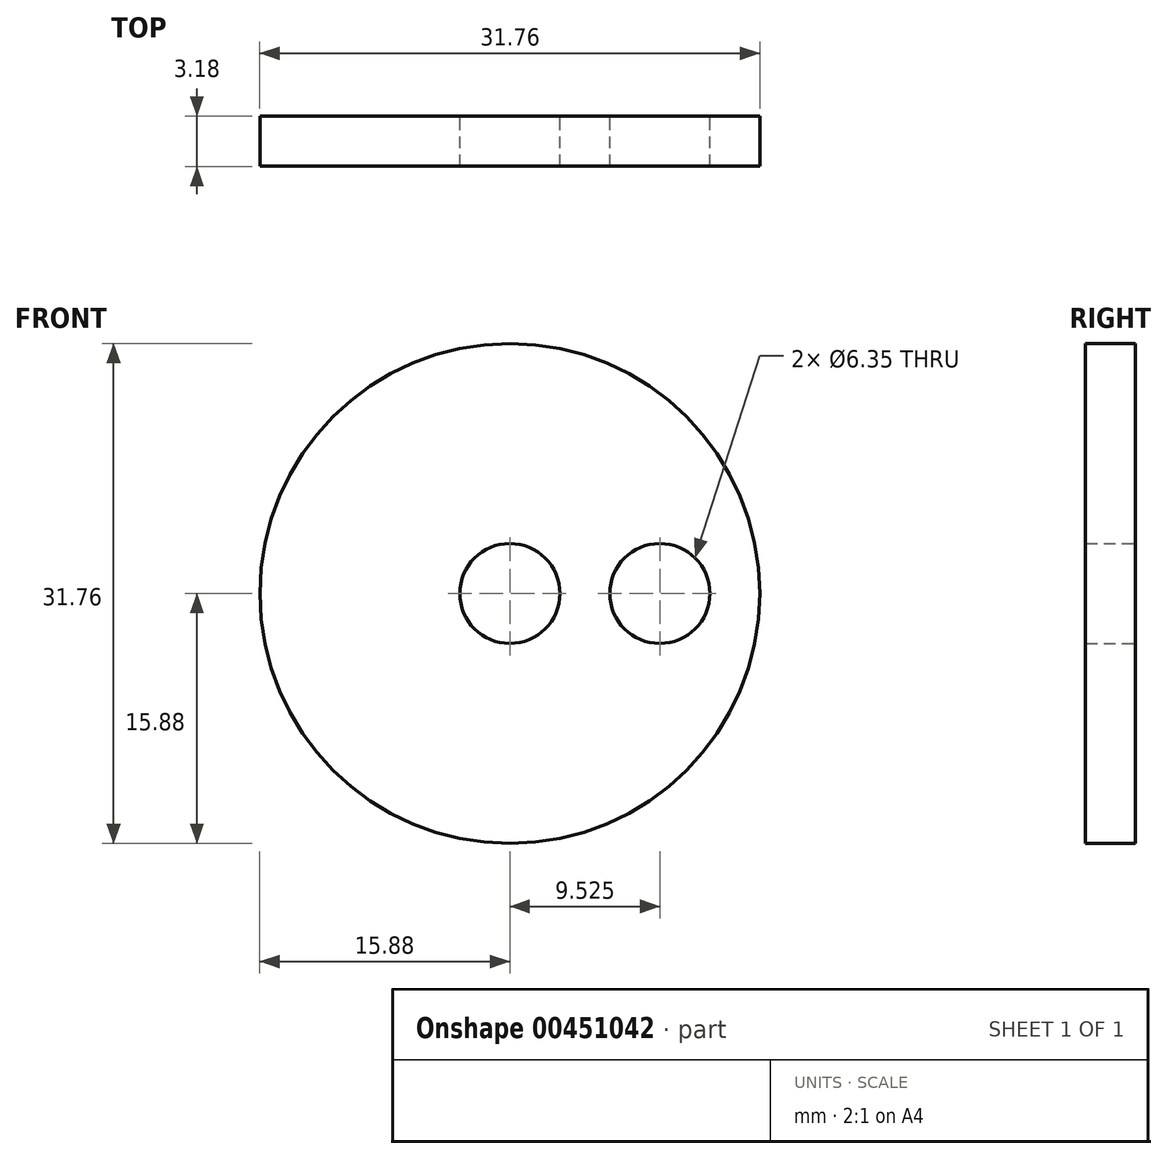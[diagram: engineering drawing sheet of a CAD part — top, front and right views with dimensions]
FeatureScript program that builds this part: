
annotation { "Feature Type Name" : "Feature", "Feature Type Description" : "" }
export const myFeature = defineFeature(function(context is Context, id is Id, definition is map)
    precondition{}
    {
        {
            var Q0;
            Q0=qCreatedBy(makeId("Front.planeOp"),FACE);
            var sketch = newSketch(context, id + "F0", { "sketchPlane" : qUnion([Q0])});
            skCircle(sketch, "E0", {"center": v(0, 0) * mm, "radius": 15.88 * mm});
            skCircle(sketch, "E1", {"center": v(0, 0) * mm, "radius": 3.18 * mm});
            skLineSegment(sketch, "E2", {"start": v(3.18, 0) * mm, "end": v(15.88, 0) * mm, "construction": true});
            skCircle(sketch, "E3", {"center": v(9.53, 0) * mm, "radius": 3.18 * mm});
            skSolve(sketch);
        }
        {
            var Q0;
            Q0 = qSketchRegion(id + "F0", true);
            extrude(context, id + "F1", {"entities" : qUnion([Q0]), "depth" : 3.17 * mm});
        }
    });
